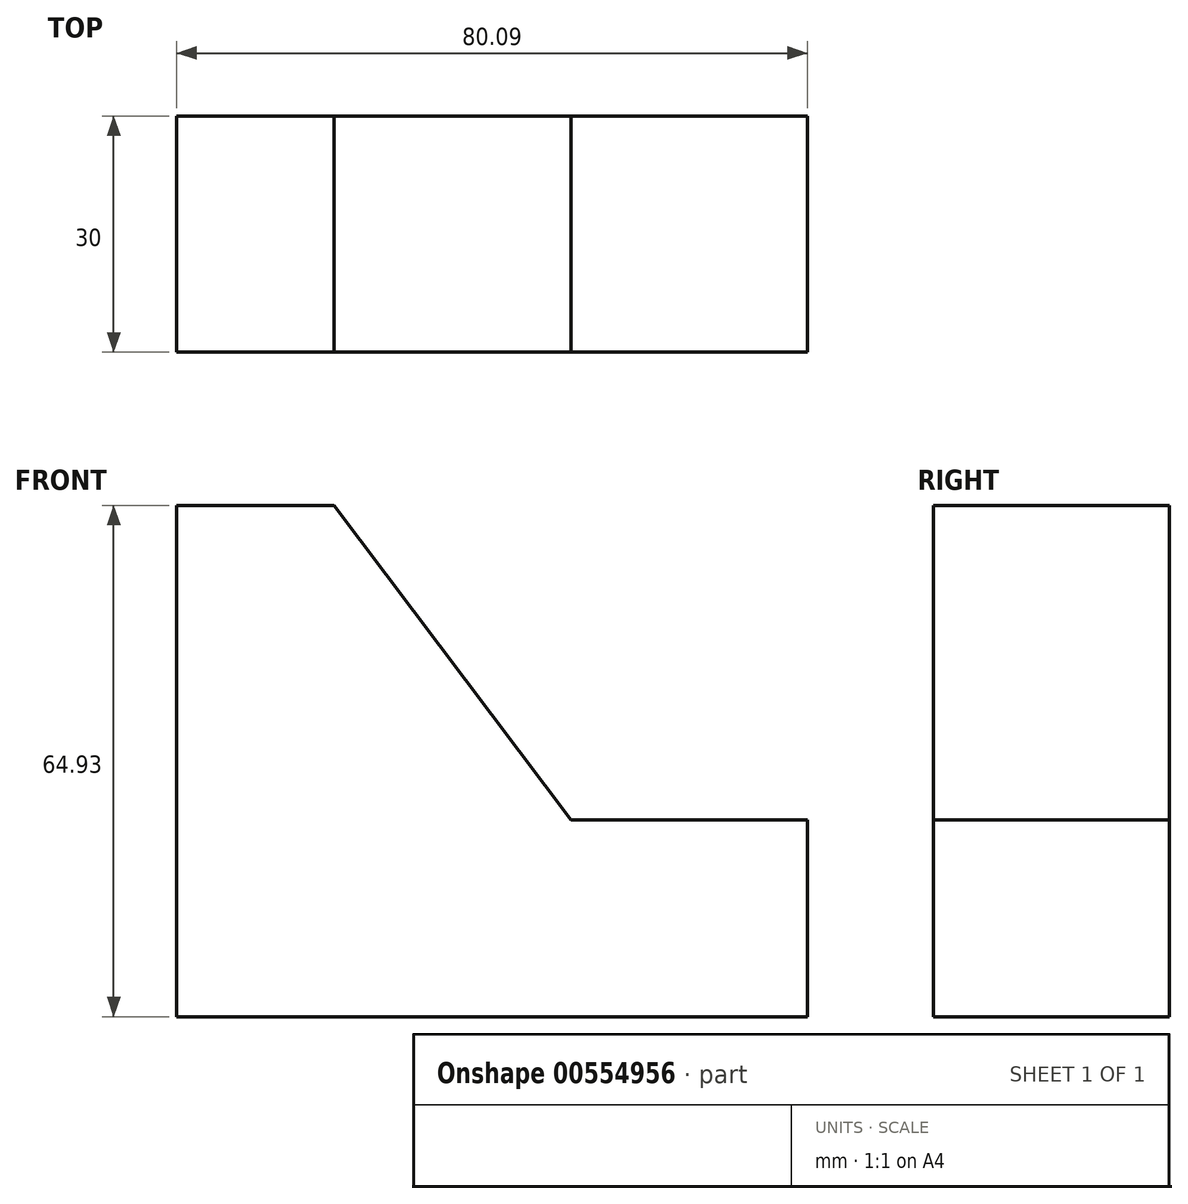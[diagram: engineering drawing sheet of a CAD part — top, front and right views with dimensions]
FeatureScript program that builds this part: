
annotation { "Feature Type Name" : "Feature", "Feature Type Description" : "" }
export const myFeature = defineFeature(function(context is Context, id is Id, definition is map)
    precondition{}
    {
        {
            var Q0;
            Q0=qCreatedBy(makeId("Front.planeOp"),FACE);
            var sketch = newSketch(context, id + "F0", { "sketchPlane" : qUnion([Q0])});
            skLineSegment(sketch, "E0", {"start": v(0, 0) * mm, "end": v(0, 64.93) * mm});
            skLineSegment(sketch, "E1", {"start": v(0, 64.93) * mm, "end": v(20, 64.93) * mm});
            skLineSegment(sketch, "E2", {"start": v(20, 64.93) * mm, "end": v(50.1, 25) * mm});
            skLineSegment(sketch, "E3", {"start": v(50.1, 25) * mm, "end": v(80.1, 25) * mm});
            skLineSegment(sketch, "E4", {"start": v(80.1, 25) * mm, "end": v(80.1, 0) * mm});
            skLineSegment(sketch, "E5", {"start": v(80.1, 0) * mm, "end": v(0, 0) * mm});
            skLineSegment(sketch, "E6", {"start": v(50.1, 25) * mm, "end": v(0, 25) * mm, "construction": true});
            skLineSegment(sketch, "E7", {"start": v(20, 64.93) * mm, "end": v(20, 0) * mm, "construction": true});
            skSolve(sketch);
        }
        {
            var Q0;
            Q0 = qSketchRegion(id + "F0", true);
            extrude(context, id + "F1", {"entities" : qUnion([Q0]), "depth" : 30 * mm, "offsetDistance" : 25 * mm});
        }
    });
